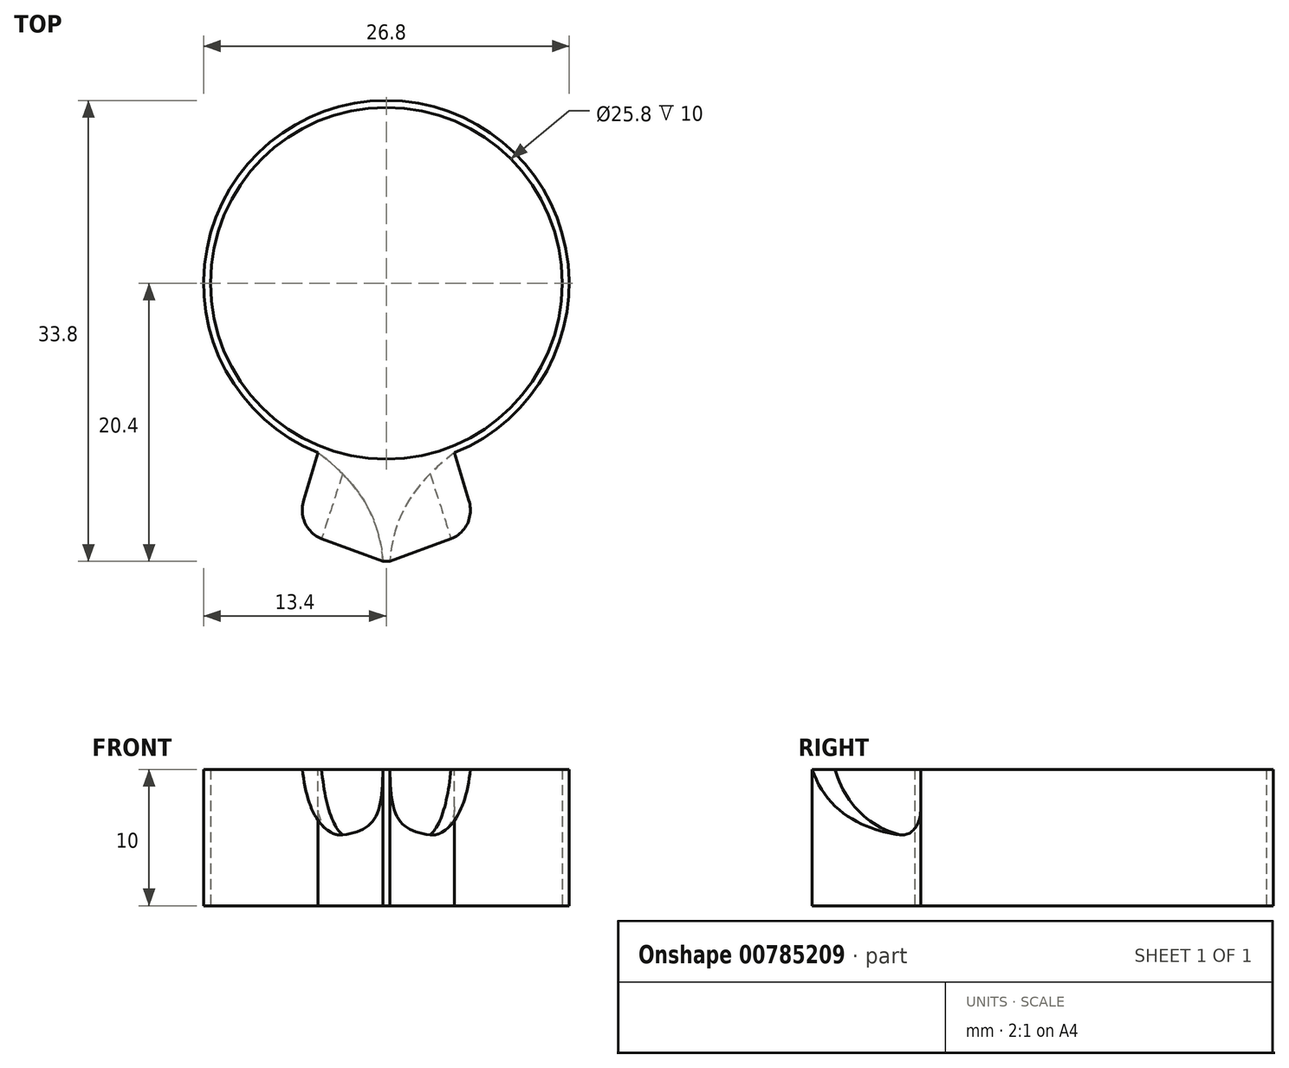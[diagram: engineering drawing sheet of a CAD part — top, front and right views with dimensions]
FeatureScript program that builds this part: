
annotation { "Feature Type Name" : "Feature", "Feature Type Description" : "" }
export const myFeature = defineFeature(function(context is Context, id is Id, definition is map)
    precondition{}
    {
        {
            var Q0;
            Q0=qCreatedBy(makeId("Top.planeOp"),FACE);
            var sketch = newSketch(context, id + "F0", { "sketchPlane" : qUnion([Q0])});
            skCircle(sketch, "E0", {"center": v(0, 0) * mm, "radius": 12.9 * mm});
            skCircle(sketch, "E1", {"center": v(0, 0) * mm, "radius": 13.4 * mm});
            skSolve(sketch);
        }
        {
            var Q0;
            Q0 = qSketchRegion(id + "F0", true);
            extrude(context, id + "F1", {"entities" : qUnion([Q0]), "depth" : 10 * mm, "offsetDistance" : 25 * mm});
        }
        {
            var Q0;
            Q0=makeQuery(id+"F1.opExtrude","CAP_FACE",FACE,{"disambiguationData":[OSD([sQuery(id+"F0.wireOp",EDGE,"E0"),sQuery(id+"F0.wireOp",EDGE,"E1")])],"isStart":false});
            var sketch = newSketch(context, id + "F2", { "sketchPlane" : qUnion([Q0])});
            skLineSegment(sketch, "E2", {"start": v(0, -13.4) * mm, "end": v(-7.41, -13.4) * mm, "construction": true});
            skLineSegment(sketch, "E3", {"start": v(-7.41, -13.4) * mm, "end": v(8.16, -13.4) * mm, "construction": true});
            skLineSegment(sketch, "E4", {"start": v(-5, -13.4) * mm, "end": v(-5, -12.43) * mm, "construction": true});
            skLineSegment(sketch, "E5", {"start": v(5, -13.4) * mm, "end": v(5, -12.43) * mm, "construction": true});
            skLineSegment(sketch, "E6", {"start": v(0, -20.4) * mm, "end": v(-0.25, -20.4) * mm});
            skFitSpline(sketch, "E7", {"points": [v(-5, -12.43) * mm, v(-0.25, -20.4) * mm], "startDerivative": vector(7.68, -5.77) * mm, "endDerivative": vector(0.8, -11.05) * mm});
            skLineSegment(sketch, "E8", {"start": v(0, -20.4) * mm, "end": v(0, -13.4) * mm});
            skFitSpline(sketch, "E9.MirrorCS", {"points": [v(5, -12.43) * mm, v(0.25, -20.4) * mm], "startDerivative": vector(-7.68, -5.77) * mm, "endDerivative": vector(-0.8, -11.05) * mm});
            skLineSegment(sketch, "E10.MirrorCS", {"start": v(0, -20.4) * mm, "end": v(0.25, -20.4) * mm});
            skSolve(sketch);
        }
        {
            var Q0;
            Q0=makeQuery(id+"F2.imprint","IMPRINT",FACE,{"disambiguationData":[TD([[makeQuery(id+"F2.imprint","IMPRINT",EDGE,{"derivedFrom":sQuery(id+"F2.wireOp",EDGE,"E6")}),-1.0]])]});
            var Q1;
            {var subQ0=sQuery(id+"F2.wireOp",EDGE,"E8");Q1=makeQuery(id+"F2.imprint","IMPRINT",FACE,{"disambiguationData":[TD([[makeQuery(id+"F2.imprint","IMPRINT",EDGE,{"derivedFrom":subQ0}),-1.0]])]});}
            extrude(context, id + "F3", {"entities" : qUnion([Q0, Q1]), "operationType" : NewBodyOperationType.ADD, "depth" : -10 * mm, "offsetDistance" : 25 * mm});
        }
        {
            var Q0;
            {var subQ0=sQuery(id+"F0.wireOp",EDGE,"E1");Q0=makeQuery(id+"F3.boolean.opBoolean","MERGE",FACE,{"derivedFrom":[makeQuery(id+"F1.opExtrude","CAP_FACE",FACE,{"disambiguationData":[OSD([sQuery(id+"F0.wireOp",EDGE,"E0"),subQ0])],"isStart":false}),makeQuery(id+"F3.opExtrude","CAP_FACE",FACE,{"disambiguationData":[OSD([subQ0,sQuery(id+"F2.wireOp",EDGE,"E6"),sQuery(id+"F2.wireOp",EDGE,"E7"),sQuery(id+"F2.wireOp",EDGE,"E9.MirrorCS"),sQuery(id+"F2.wireOp",EDGE,"E10.MirrorCS")])],"isStart":true})]});}
            var sketch = newSketch(context, id + "F4", { "sketchPlane" : qUnion([Q0])});
            skLineSegment(sketch, "E11", {"start": v(-0.25, -20.4) * mm, "end": v(-6.69, -18.02) * mm});
            skLineSegment(sketch, "E12", {"start": v(-6.69, -18.02) * mm, "end": v(-5, -12.43) * mm});
            skLineSegment(sketch, "E13.MirrorCS", {"start": v(0.25, -20.4) * mm, "end": v(6.69, -18.02) * mm});
            skLineSegment(sketch, "E14.MirrorCS", {"start": v(6.69, -18.02) * mm, "end": v(5, -12.43) * mm});
            skSolve(sketch);
        }
        {
            var Q0;
            Q0=makeQuery(id+"F4.imprint","IMPRINT",FACE,{"disambiguationData":[TD([[makeQuery(id+"F4.imprint","IMPRINT",EDGE,{"derivedFrom":sQuery(id+"F4.wireOp",EDGE,"E11")}),-1.0]])]});
            extrude(context, id + "F5", {"entities" : qUnion([Q0]), "operationType" : NewBodyOperationType.ADD, "depth" : -5 * mm, "offsetDistance" : 25 * mm});
        }
        {
            var Q0;
            Q0=makeQuery(id+"F4.imprint","IMPRINT",FACE,{"disambiguationData":[TD([[makeQuery(id+"F4.imprint","IMPRINT",EDGE,{"derivedFrom":sQuery(id+"F4.wireOp",EDGE,"E13.MirrorCS")}),1.0]])]});
            extrude(context, id + "F6", {"entities" : qUnion([Q0]), "operationType" : NewBodyOperationType.ADD, "depth" : -5 * mm, "offsetDistance" : 25 * mm});
        }
        {
            var Q0;
            Q0=makeQuery(id+"F5.opExtrude","CAP_EDGE",EDGE,{"disambiguationData":[OSD([sQuery(id+"F4.wireOp",EDGE,"E11")])],"isStart":false});
            var Q1;
            Q1=makeQuery(id+"F6.opExtrude","CAP_EDGE",EDGE,{"disambiguationData":[OSD([sQuery(id+"F4.wireOp",EDGE,"E13.MirrorCS")])],"isStart":false});
            fillet(context, id + "F7", {"entities" : qUnion([Q0, Q1]), "radius" : 6.88 * mm, "tangentPropagation" : true, "allowEdgeOverflow" : false});
        }
        {
            var Q0;
            Q0=makeQuery(id+"F7.opFillet","BLEND_EDGE",EDGE,{"blendedFrom":[makeQuery(id+"F5.opExtrude","CAP_EDGE",EDGE,{"disambiguationData":[OSD([sQuery(id+"F4.wireOp",EDGE,"E11")])],"isStart":false}),makeQuery(id+"F5.opExtrude","SWEPT_FACE",FACE,{"disambiguationData":[OSD([sQuery(id+"F4.wireOp",EDGE,"E12")])]})],"blendedInto":[makeQuery(id+"F5.opExtrude","SWEPT_FACE",FACE,{"disambiguationData":[OSD([sQuery(id+"F4.wireOp",EDGE,"E12")])]})]});
            var Q1;
            Q1=makeQuery(id+"F7.opFillet","BLEND_EDGE",EDGE,{"blendedFrom":[makeQuery(id+"F6.opExtrude","CAP_EDGE",EDGE,{"disambiguationData":[OSD([sQuery(id+"F4.wireOp",EDGE,"E13.MirrorCS")])],"isStart":false}),makeQuery(id+"F6.opExtrude","SWEPT_FACE",FACE,{"disambiguationData":[OSD([sQuery(id+"F4.wireOp",EDGE,"E14.MirrorCS")])]})],"blendedInto":[makeQuery(id+"F6.opExtrude","SWEPT_FACE",FACE,{"disambiguationData":[OSD([sQuery(id+"F4.wireOp",EDGE,"E14.MirrorCS")])]})]});
            fillet(context, id + "F8", {"entities" : qUnion([Q0, Q1]), "radius" : 2.2 * mm, "tangentPropagation" : true, "allowEdgeOverflow" : false});
        }
    });
